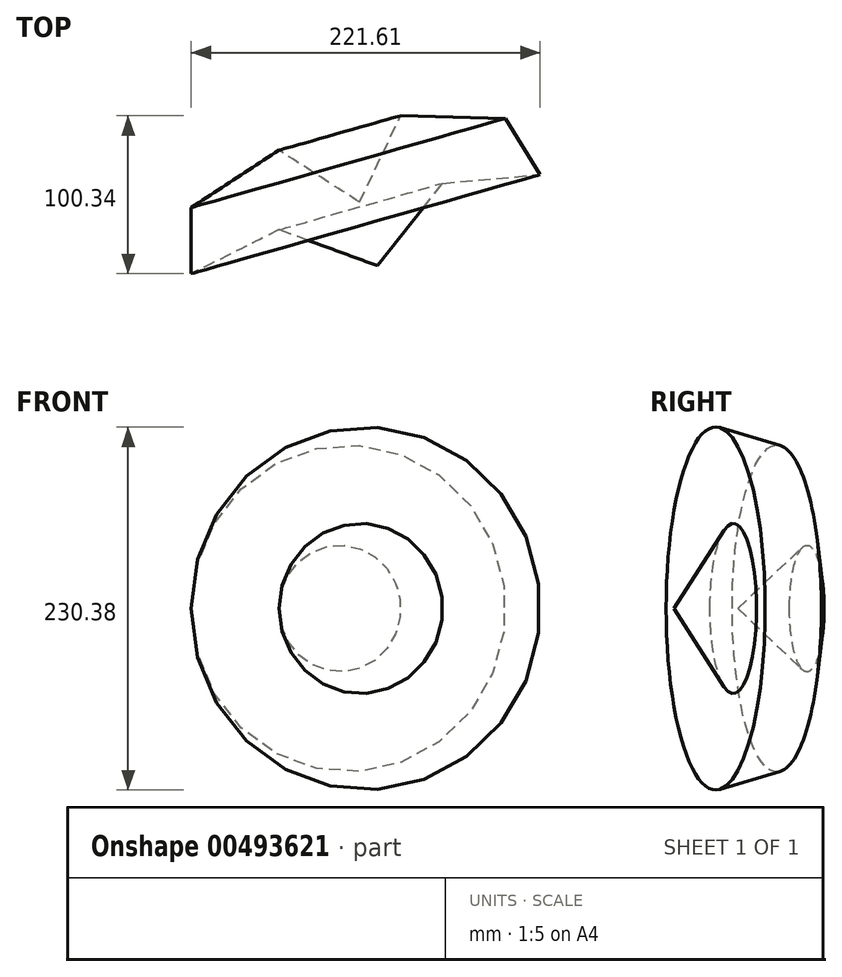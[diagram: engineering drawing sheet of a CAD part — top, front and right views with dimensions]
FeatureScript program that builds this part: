
annotation { "Feature Type Name" : "Feature", "Feature Type Description" : "" }
export const myFeature = defineFeature(function(context is Context, id is Id, definition is map)
    precondition{}
    {
        {
            var Q0;
            Q0=qCreatedBy(makeId("Top.planeOp"),FACE);
            var sketch = newSketch(context, id + "F0", { "sketchPlane" : qUnion([Q0])});
            skLineSegment(sketch, "E0", {"start": v(-55.7, -27.86) * mm, "end": v(-55.7, 14.07) * mm});
            skLineSegment(sketch, "E1", {"start": v(-55.7, 14.07) * mm, "end": v(0, 50.52) * mm});
            skLineSegment(sketch, "E2", {"start": v(0, 50.52) * mm, "end": v(51.14, 17.57) * mm});
            skLineSegment(sketch, "E3", {"start": v(51.14, 17.57) * mm, "end": v(62.62, -22.87) * mm});
            skLineSegment(sketch, "E4", {"start": v(62.62, -22.87) * mm, "end": v(0, 0) * mm});
            skLineSegment(sketch, "E5", {"start": v(0, 0) * mm, "end": v(-55.7, -27.86) * mm});
            skSolve(sketch);
        }
        {
            var Q0;
            Q0=makeQuery(id+"F0.imprint","IMPRINT",FACE,{"disambiguationData":[TD([[makeQuery(id+"F0.imprint","IMPRINT",EDGE,{"derivedFrom":sQuery(id+"F0.wireOp",EDGE,"E0")}),-1.0]])]});
            var Q1;
            Q1=sQuery(id+"F0.wireOp",EDGE,"E3");
            revolve(context, id + "F1", {"entities" : qUnion([Q0]), "axis" : qUnion([Q1]), "revolveType" : RevolveType.FULL});
        }
    });
